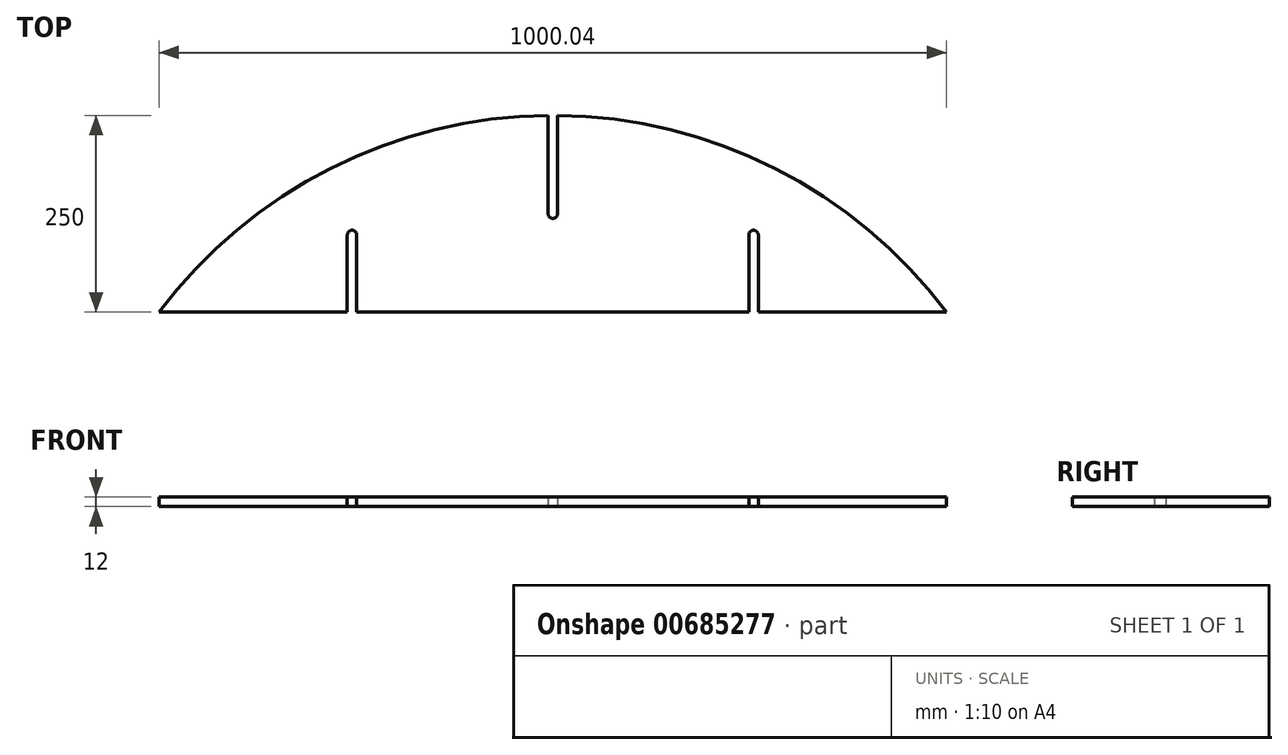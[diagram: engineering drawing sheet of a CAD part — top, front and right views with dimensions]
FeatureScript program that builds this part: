
annotation { "Feature Type Name" : "Feature", "Feature Type Description" : "" }
export const myFeature = defineFeature(function(context is Context, id is Id, definition is map)
    precondition{}
    {
        {
            var Q0;
            Q0=qCreatedBy(makeId("Top.planeOp"),FACE);
            var sketch = newSketch(context, id + "F0", { "sketchPlane" : qUnion([Q0])});
            skLineSegment(sketch, "E0", {"start": v(0, 0) * mm, "end": v(239.02, 0) * mm});
            skArc(sketch, "E1", {"start": v(1000.04, 0) * mm, "mid": v(782.23, 182.69) * mm, "end": v(506.02, 250) * mm});
            skLineSegment(sketch, "E2", {"start": v(500.02, 0) * mm, "end": v(500.02, 137.45) * mm, "construction": true});
            skLineSegment(sketch, "E3", {"start": v(494.02, 250) * mm, "end": v(494.02, 125) * mm});
            skLineSegment(sketch, "E4", {"start": v(506.02, 125) * mm, "end": v(506.02, 250) * mm});
            skArc(sketch, "E5.trimOffspring", {"start": v(494.02, 250) * mm, "mid": v(217.82, 182.69) * mm, "end": v(0, 0) * mm});
            skLineSegment(sketch, "E6", {"start": v(749.02, 98) * mm, "end": v(749.02, 0) * mm});
            skLineSegment(sketch, "E7", {"start": v(761.02, 98) * mm, "end": v(761.02, 0) * mm});
            skLineSegment(sketch, "E8.trimOffspring", {"start": v(761.02, 0) * mm, "end": v(1000.04, 0) * mm});
            skLineSegment(sketch, "E9", {"start": v(755.02, 132.8) * mm, "end": v(755.02, -62.61) * mm, "construction": true});
            skLineSegment(sketch, "E10.MirrorCS", {"start": v(239.02, 98) * mm, "end": v(239.02, 0) * mm});
            skLineSegment(sketch, "E11.MirrorCS", {"start": v(251.02, 98) * mm, "end": v(251.02, 0) * mm});
            skLineSegment(sketch, "E12.trimOffspring", {"start": v(251.02, 0) * mm, "end": v(749.02, 0) * mm});
            skArc(sketch, "E13", {"start": v(761.02, 98) * mm, "mid": v(755.02, 104) * mm, "end": v(749.02, 98) * mm});
            skArc(sketch, "E14", {"start": v(494.02, 125) * mm, "mid": v(500.02, 119) * mm, "end": v(506.02, 125) * mm});
            skArc(sketch, "E15", {"start": v(251.02, 98) * mm, "mid": v(245.02, 104) * mm, "end": v(239.02, 98) * mm});
            skSolve(sketch);
        }
        {
            var Q0;
            Q0=qSketchRegion(id+"F0",true);
            extrude(context, id + "F1", {"entities" : qUnion([Q0]), "depth" : 12 * mm, "offsetDistance" : 25 * mm});
        }
    });
